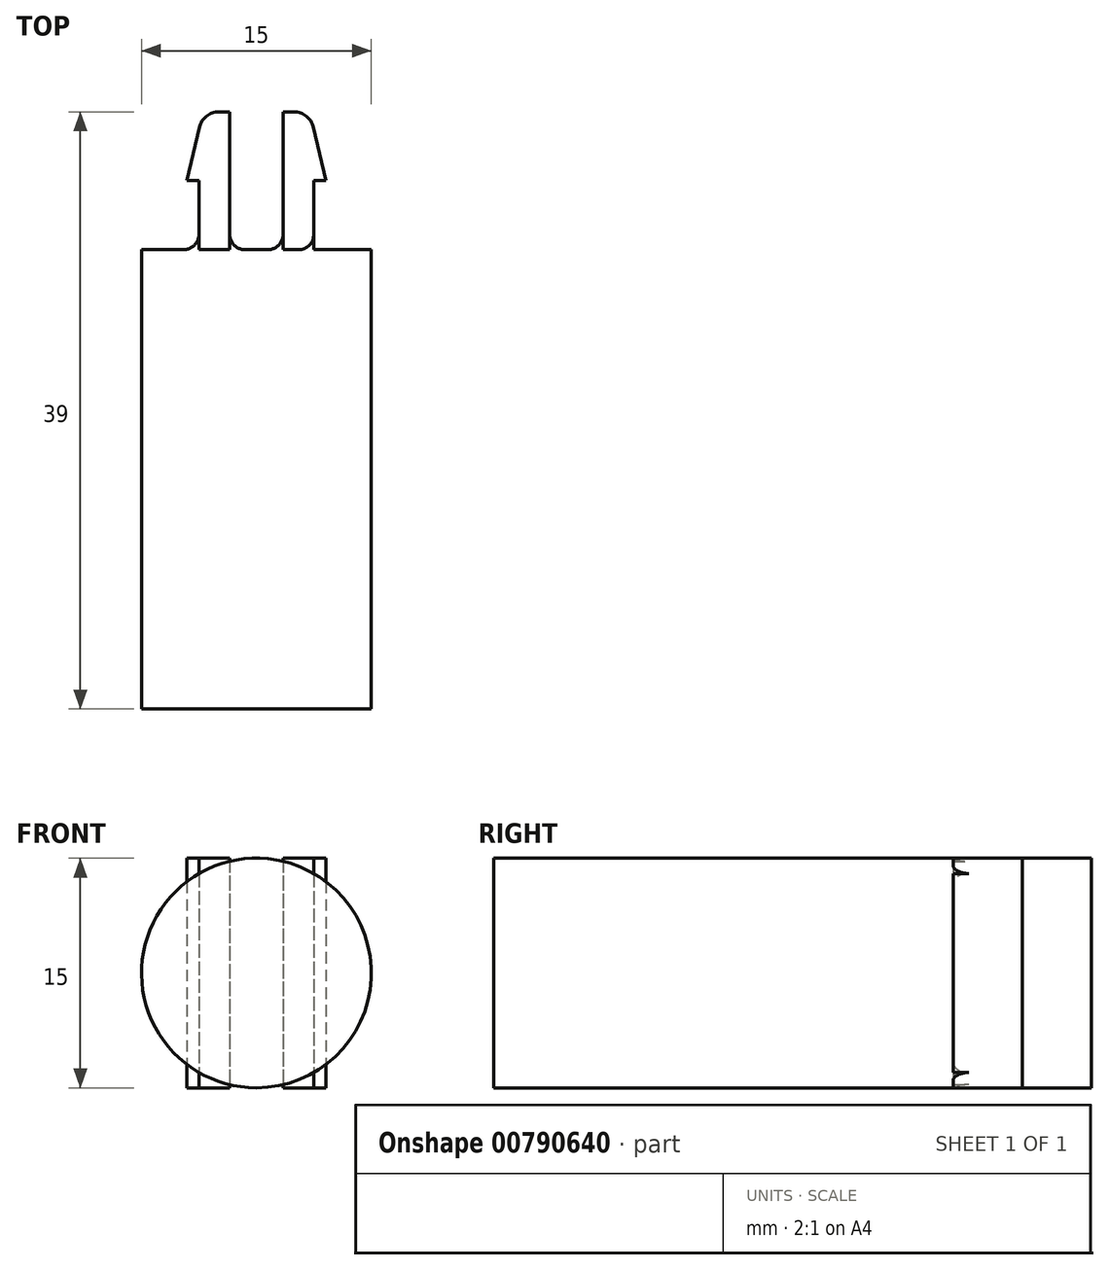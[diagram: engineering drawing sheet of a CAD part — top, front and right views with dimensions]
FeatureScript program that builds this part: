
annotation { "Feature Type Name" : "Feature", "Feature Type Description" : "" }
export const myFeature = defineFeature(function(context is Context, id is Id, definition is map)
    precondition{}
    {
        {
            var Q0;
            Q0=qCreatedBy(makeId("Top.planeOp"),FACE);
            var sketch = newSketch(context, id + "F0", { "sketchPlane" : qUnion([Q0])});
            skLineSegment(sketch, "E0.bottom", {"start": v(-1.75, 0) * mm, "end": v(1.75, 0) * mm});
            skLineSegment(sketch, "E0.left", {"start": v(-1.75, 0) * mm, "end": v(-1.75, 9) * mm});
            skLineSegment(sketch, "E0.right", {"start": v(1.75, 0) * mm, "end": v(1.75, 9) * mm});
            skLineSegment(sketch, "E1.bottom", {"start": v(1.75, 9) * mm, "end": v(2.45, 9) * mm});
            skLineSegment(sketch, "E1.top", {"start": v(1.75, 0) * mm, "end": v(3.75, 0) * mm});
            skLineSegment(sketch, "E1.left", {"start": v(1.75, 9) * mm, "end": v(1.75, 0) * mm});
            skLineSegment(sketch, "E1.right", {"start": v(3.75, 7.7) * mm, "end": v(3.75, 0) * mm});
            skLineSegment(sketch, "E2.bottom", {"start": v(-1.75, 9) * mm, "end": v(-2.45, 9) * mm});
            skLineSegment(sketch, "E2.top", {"start": v(-1.75, 0) * mm, "end": v(-3.75, 0) * mm});
            skLineSegment(sketch, "E2.left", {"start": v(-1.75, 9) * mm, "end": v(-1.75, 0) * mm});
            skLineSegment(sketch, "E2.right", {"start": v(-3.75, 7.7) * mm, "end": v(-3.75, 0) * mm});
            skPoint(sketch, "E3.visualSharp", {"position": v(3.75, 9) * mm});
            skArc(sketch, "E3.filletArc", {"start": v(3.75, 7.7) * mm, "mid": v(3.37, 8.62) * mm, "end": v(2.45, 9) * mm});
            skPoint(sketch, "E4.visualSharp", {"position": v(-3.75, 9) * mm});
            skArc(sketch, "E4.filletArc", {"start": v(-2.45, 9) * mm, "mid": v(-3.37, 8.62) * mm, "end": v(-3.75, 7.7) * mm});
            skLineSegment(sketch, "E5", {"start": v(3.71, 8) * mm, "end": v(4.55, 4.5) * mm});
            skLineSegment(sketch, "E6", {"start": v(4.55, 4.5) * mm, "end": v(3.75, 4.5) * mm});
            skLineSegment(sketch, "E7.MirrorCS", {"start": v(-3.71, 8) * mm, "end": v(-4.55, 4.5) * mm});
            skLineSegment(sketch, "E8.MirrorCS", {"start": v(-4.55, 4.5) * mm, "end": v(-3.75, 4.5) * mm});
            skSolve(sketch);
        }
        {
            var Q0;
            {var subQ5=sQuery(id+"F0.wireOp",EDGE,"E2.bottom");Q0=makeQuery(id+"F0.imprint","IMPRINT",FACE,{"disambiguationData":[TD([[makeQuery(id+"F0.imprint","IMPRINT",EDGE,{"derivedFrom":subQ5}),1.0]])]});}
            var Q1;
            {var subQ4=sQuery(id+"F0.wireOp",EDGE,"E7.MirrorCS");Q1=makeQuery(id+"F0.imprint","IMPRINT",FACE,{"disambiguationData":[TD([[makeQuery(id+"F0.imprint","IMPRINT",EDGE,{"derivedFrom":subQ4}),1.0]])]});}
            var Q2;
            {var subQ4=sQuery(id+"F0.wireOp",EDGE,"E5");Q2=makeQuery(id+"F0.imprint","IMPRINT",FACE,{"disambiguationData":[TD([[makeQuery(id+"F0.imprint","IMPRINT",EDGE,{"derivedFrom":subQ4}),-1.0]])]});}
            var Q3;
            {var subQ5=sQuery(id+"F0.wireOp",EDGE,"E1.bottom");Q3=makeQuery(id+"F0.imprint","IMPRINT",FACE,{"disambiguationData":[TD([[makeQuery(id+"F0.imprint","IMPRINT",EDGE,{"derivedFrom":subQ5}),-1.0]])]});}
            extrude(context, id + "F1", {"entities" : qUnion([Q0, Q1, Q2, Q3]), "endBound" : BoundingType.SYMMETRIC, "depth" : 15 * mm, "offsetDistance" : 25 * mm});
        }
        {
            var Q0;
            Q0=qCreatedBy(makeId("Front.planeOp"),FACE);
            var sketch = newSketch(context, id + "F2", { "sketchPlane" : qUnion([Q0])});
            skCircle(sketch, "E9", {"center": v(0, 0) * mm, "radius": 7.5 * mm});
            skSolve(sketch);
        }
        {
            var Q0;
            Q0=makeQuery(id+"F2.imprint","IMPRINT",FACE,{"disambiguationData":[TD([[makeQuery(id+"F2.imprint","IMPRINT",EDGE,{"derivedFrom":sQuery(id+"F2.wireOp",EDGE,"E9")}),1.0]])]});
            extrude(context, id + "F3", {"entities" : qUnion([Q0]), "operationType" : NewBodyOperationType.ADD, "depth" : 30 * mm, "offsetDistance" : 25 * mm});
        }
        {
            var Q0;
            {var subQ0=sQuery(id+"F0.wireOp",EDGE,"E1.right");Q0=makeQuery(id+"F3.boolean.opBoolean","SPLIT",EDGE,{"disambiguationData":[topologyDisambiguationEdgeConnected([makeQuery(id+"F1.opExtrude","SWEPT_FACE",FACE,{"disambiguationData":[OSD([subQ0])]}),makeQuery(id+"F3.opExtrude","CAP_FACE",FACE,{"disambiguationData":[OSD([sQuery(id+"F2.wireOp",EDGE,"E9")])],"isStart":true})])],"derivedFrom":makeQuery(id+"F1.opExtrude","SWEPT_EDGE",EDGE,{"disambiguationData":[OSD([sQuery(id+"F0.wireOp",EDGE,"E1.top"),subQ0])]})});}
            var Q1;
            {var subQ0=sQuery(id+"F0.wireOp",EDGE,"E2.left");Q1=makeQuery(id+"F3.boolean.opBoolean","SPLIT",EDGE,{"disambiguationData":[topologyDisambiguationEdgeConnected([makeQuery(id+"F1.opExtrude","SWEPT_FACE",FACE,{"disambiguationData":[OSD([subQ0])]}),makeQuery(id+"F3.opExtrude","CAP_FACE",FACE,{"disambiguationData":[OSD([sQuery(id+"F2.wireOp",EDGE,"E9")])],"isStart":true})])],"derivedFrom":makeQuery(id+"F1.opExtrude","SWEPT_EDGE",EDGE,{"disambiguationData":[OSD([sQuery(id+"F0.wireOp",EDGE,"E2.top"),subQ0])]})});}
            var Q2;
            {var subQ0=sQuery(id+"F0.wireOp",EDGE,"E1.left");Q2=makeQuery(id+"F3.boolean.opBoolean","SPLIT",EDGE,{"disambiguationData":[topologyDisambiguationEdgeConnected([makeQuery(id+"F1.opExtrude","SWEPT_FACE",FACE,{"disambiguationData":[OSD([subQ0])]}),makeQuery(id+"F3.opExtrude","CAP_FACE",FACE,{"disambiguationData":[OSD([sQuery(id+"F2.wireOp",EDGE,"E9")])],"isStart":true})])],"derivedFrom":makeQuery(id+"F1.opExtrude","SWEPT_EDGE",EDGE,{"disambiguationData":[OSD([sQuery(id+"F0.wireOp",EDGE,"E1.top"),subQ0])]})});}
            var Q3;
            {var subQ0=sQuery(id+"F0.wireOp",EDGE,"E2.right");Q3=makeQuery(id+"F3.boolean.opBoolean","SPLIT",EDGE,{"disambiguationData":[topologyDisambiguationEdgeConnected([makeQuery(id+"F1.opExtrude","SWEPT_FACE",FACE,{"disambiguationData":[OSD([subQ0])]}),makeQuery(id+"F3.opExtrude","CAP_FACE",FACE,{"disambiguationData":[OSD([sQuery(id+"F2.wireOp",EDGE,"E9")])],"isStart":true})])],"derivedFrom":makeQuery(id+"F1.opExtrude","SWEPT_EDGE",EDGE,{"disambiguationData":[OSD([sQuery(id+"F0.wireOp",EDGE,"E2.top"),subQ0])]})});}
            fillet(context, id + "F4", {"entities" : qUnion([Q0, Q1, Q2, Q3]), "radius" : 1 * mm, "tangentPropagation" : true, "allowEdgeOverflow" : false});
        }
    });
